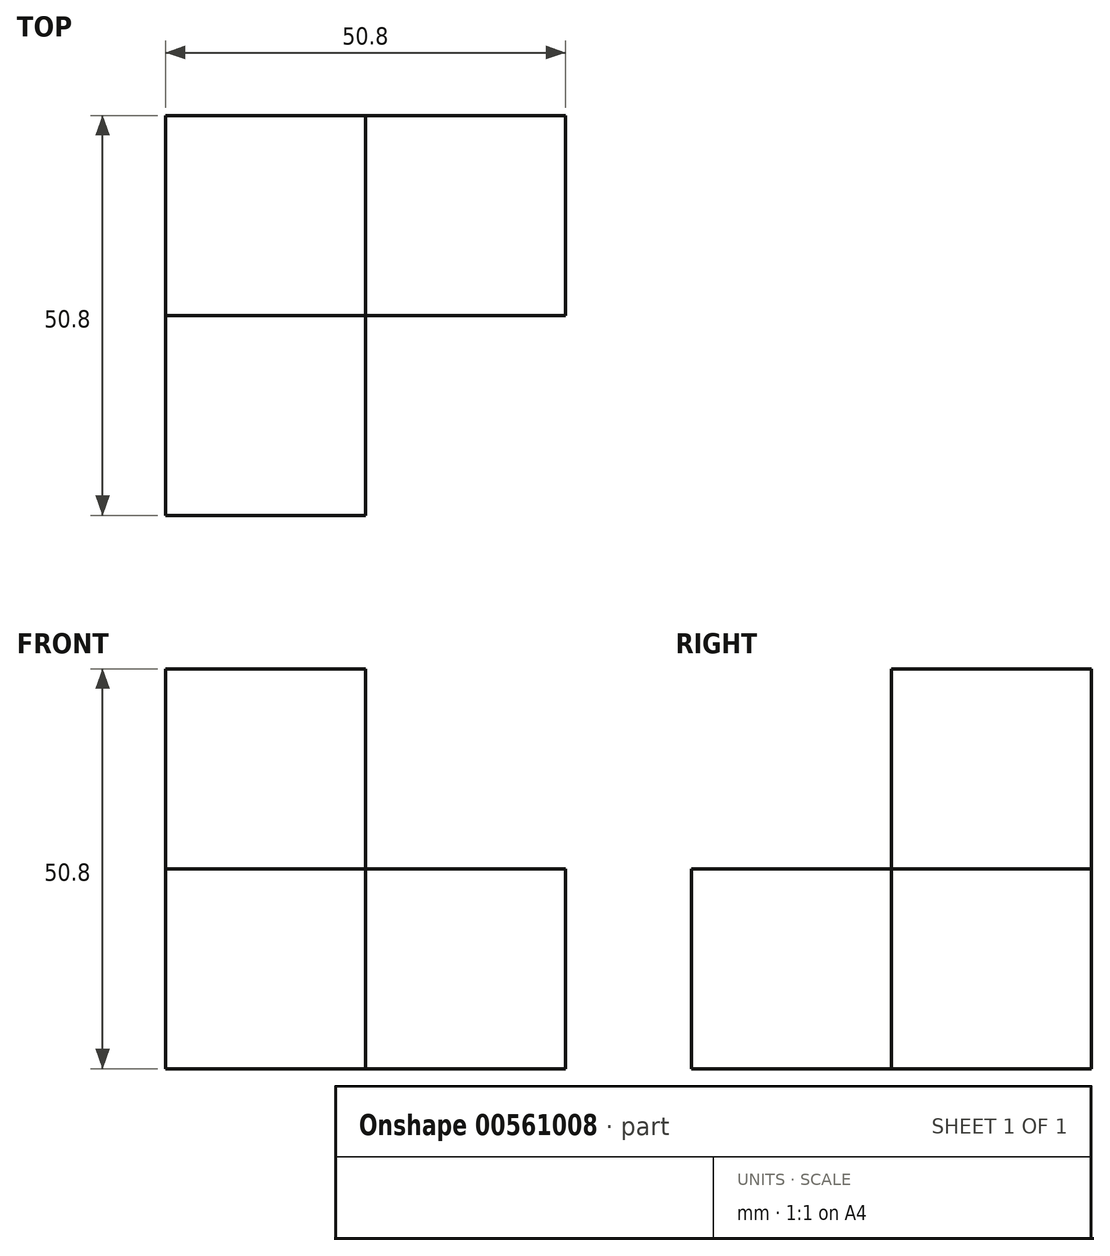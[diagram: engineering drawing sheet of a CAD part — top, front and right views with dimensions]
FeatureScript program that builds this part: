
annotation { "Feature Type Name" : "Feature", "Feature Type Description" : "" }
export const myFeature = defineFeature(function(context is Context, id is Id, definition is map)
    precondition{}
    {
        {
            var Q0;
            Q0=qCreatedBy(makeId("Front.planeOp"),FACE);
            var sketch = newSketch(context, id + "F0", { "sketchPlane" : qUnion([Q0])});
            skLineSegment(sketch, "E0.bottom", {"start": v(0, 0) * mm, "end": v(25.4, 0) * mm});
            skLineSegment(sketch, "E0.top", {"start": v(0, 25.4) * mm, "end": v(25.4, 25.4) * mm});
            skLineSegment(sketch, "E0.left", {"start": v(0, 0) * mm, "end": v(0, 25.4) * mm});
            skLineSegment(sketch, "E0.right", {"start": v(25.4, 0) * mm, "end": v(25.4, 25.4) * mm});
            skLineSegment(sketch, "E1.bottom", {"start": v(0, 25.4) * mm, "end": v(-25.4, 25.4) * mm});
            skLineSegment(sketch, "E1.top", {"start": v(0, 0) * mm, "end": v(-25.4, 0) * mm});
            skLineSegment(sketch, "E1.left", {"start": v(0, 25.4) * mm, "end": v(0, 0) * mm});
            skLineSegment(sketch, "E1.right", {"start": v(-25.4, 25.4) * mm, "end": v(-25.4, 0) * mm});
            skLineSegment(sketch, "E2.bottom", {"start": v(-25.4, 25.4) * mm, "end": v(0, 25.4) * mm});
            skLineSegment(sketch, "E2.top", {"start": v(-25.4, 50.8) * mm, "end": v(0, 50.8) * mm});
            skLineSegment(sketch, "E2.left", {"start": v(-25.4, 25.4) * mm, "end": v(-25.4, 50.8) * mm});
            skLineSegment(sketch, "E2.right", {"start": v(0, 25.4) * mm, "end": v(0, 50.8) * mm});
            skSolve(sketch);
        }
        {
            var Q0;
            Q0=makeQuery(id+"F0.imprint","IMPRINT",FACE,{"disambiguationData":[TD([[makeQuery(id+"F0.imprint","IMPRINT",EDGE,{"derivedFrom":sQuery(id+"F0.wireOp",EDGE,"E1.top")}),-1.0]])]});
            extrude(context, id + "F1", {"entities" : qUnion([Q0]), "depth" : 50.8 * mm, "offsetDistance" : 25.4 * mm});
        }
        {
            var Q0;
            Q0 = qSketchRegion(id + "F0", true);
            extrude(context, id + "F2", {"entities" : qUnion([Q0]), "depth" : 25.4 * mm, "offsetDistance" : 25.4 * mm});
        }
    });
